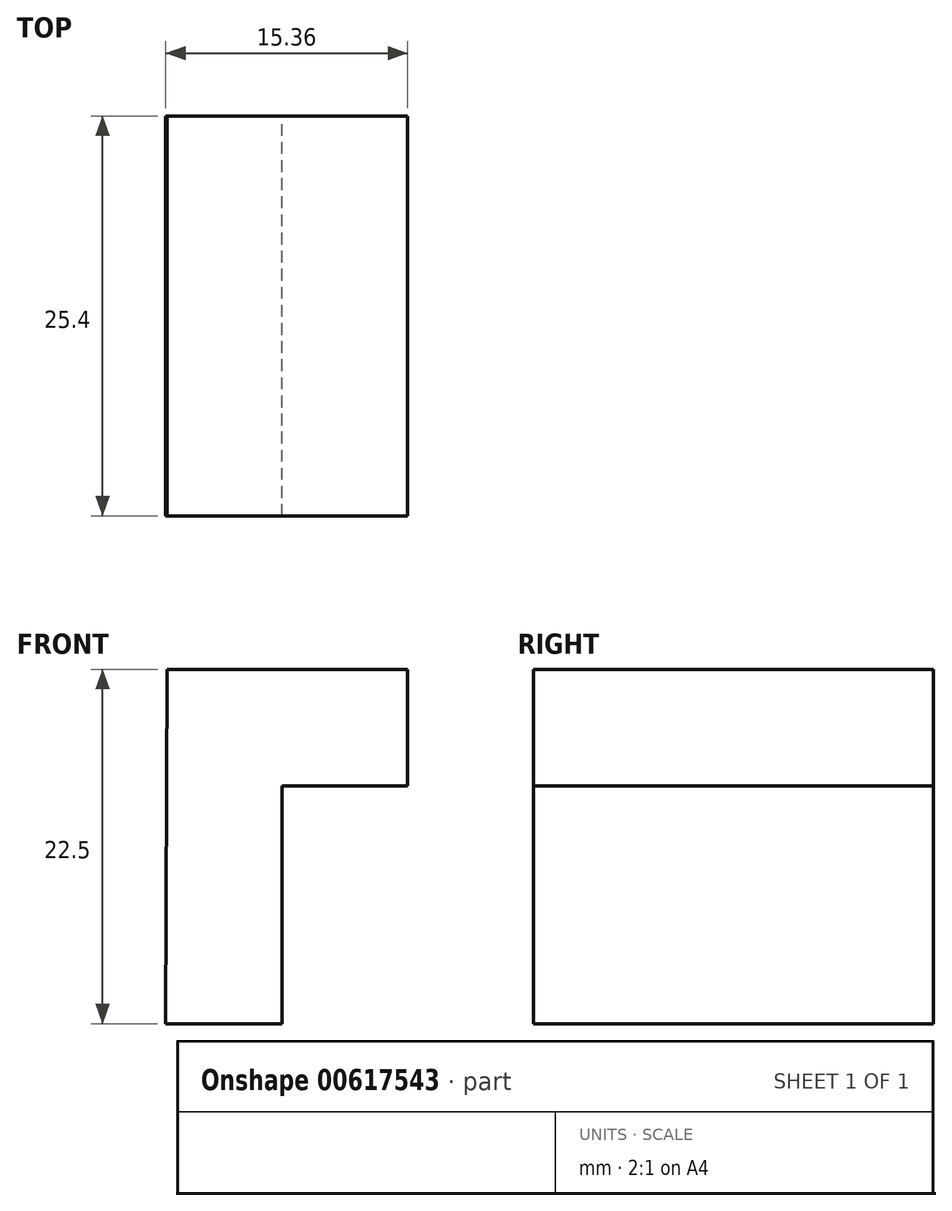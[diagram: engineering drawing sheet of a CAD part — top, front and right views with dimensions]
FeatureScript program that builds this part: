
annotation { "Feature Type Name" : "Feature", "Feature Type Description" : "" }
export const myFeature = defineFeature(function(context is Context, id is Id, definition is map)
    precondition{}
    {
        {
            var Q0;
            Q0=qCreatedBy(makeId("Front.planeOp"),FACE);
            var sketch = newSketch(context, id + "F0", { "sketchPlane" : qUnion([Q0])});
            skLineSegment(sketch, "E0", {"start": v(-17.64, 12.22) * mm, "end": v(-17.64, 27.32) * mm});
            skLineSegment(sketch, "E1", {"start": v(-17.64, 27.32) * mm, "end": v(-9.68, 27.32) * mm});
            skLineSegment(sketch, "E2", {"start": v(-9.68, 27.32) * mm, "end": v(-9.68, 34.72) * mm});
            skLineSegment(sketch, "E3", {"start": v(-17.64, 12.22) * mm, "end": v(-25.04, 12.22) * mm});
            skLineSegment(sketch, "E4", {"start": v(-9.68, 34.72) * mm, "end": v(-24.95, 34.72) * mm});
            skLineSegment(sketch, "E5", {"start": v(-24.95, 34.72) * mm, "end": v(-25.04, 12.22) * mm});
            skSolve(sketch);
        }
        {
            var Q0;
            Q0 = qSketchRegion(id + "F0", true);
            extrude(context, id + "F1", {"entities" : qUnion([Q0]), "depth" : 25.4 * mm, "offsetDistance" : 25.4 * mm});
        }
    });
